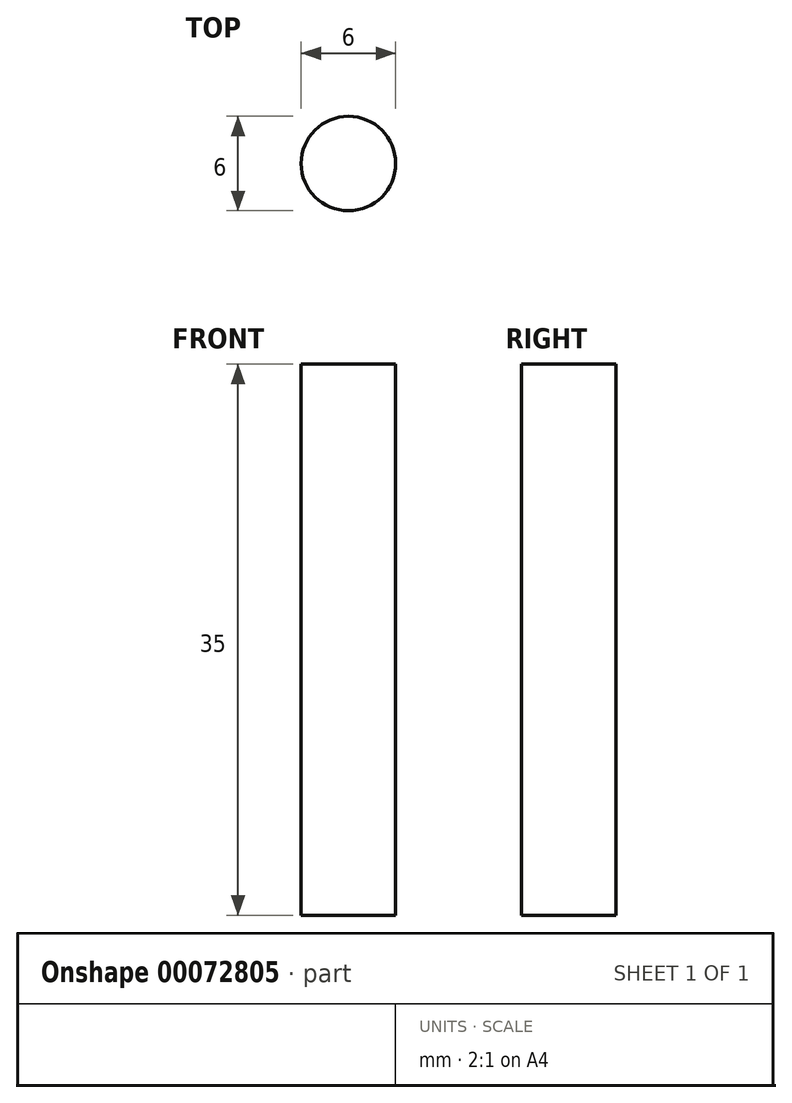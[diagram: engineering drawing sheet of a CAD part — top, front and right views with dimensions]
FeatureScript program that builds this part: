
annotation { "Feature Type Name" : "Feature", "Feature Type Description" : "" }
export const myFeature = defineFeature(function(context is Context, id is Id, definition is map)
    precondition{}
    {
        {
            var Q0;
            Q0=qCreatedBy(makeId("Top.planeOp"),FACE);
            var sketch = newSketch(context, id + "F0", { "sketchPlane" : qUnion([Q0])});
            skCircle(sketch, "E0", {"center": v(0, 0) * mm, "radius": 3 * mm});
            skSolve(sketch);
        }
        {
            var Q0;
            Q0 = qSketchRegion(id + "F0", true);
            extrude(context, id + "F1", {"entities" : qUnion([Q0]), "depth" : 35 * mm});
        }
    });
